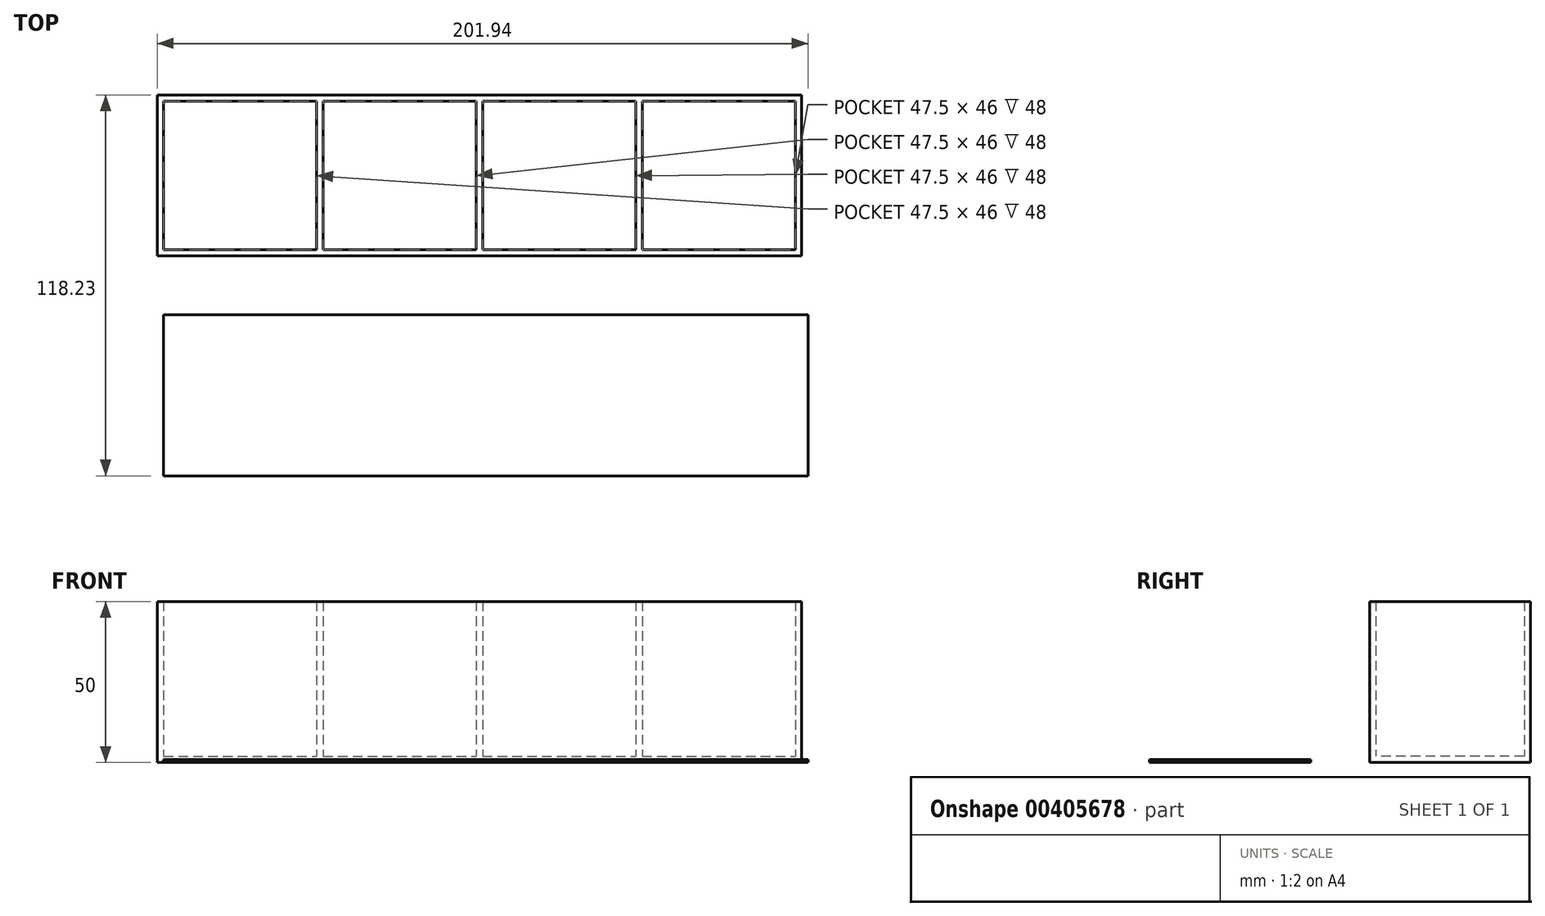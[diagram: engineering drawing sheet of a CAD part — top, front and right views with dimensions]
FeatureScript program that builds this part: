
annotation { "Feature Type Name" : "Feature", "Feature Type Description" : "" }
export const myFeature = defineFeature(function(context is Context, id is Id, definition is map)
    precondition{}
    {
        {
            var Q0;
            Q0=qCreatedBy(makeId("Top.planeOp"),FACE);
            var sketch = newSketch(context, id + "F0", { "sketchPlane" : qUnion([Q0])});
            skLineSegment(sketch, "E0.bottom", {"start": v(-100, 25) * mm, "end": v(100, 25) * mm});
            skLineSegment(sketch, "E0.top", {"start": v(-100, -25) * mm, "end": v(100, -25) * mm});
            skLineSegment(sketch, "E0.left", {"start": v(-100, 25) * mm, "end": v(-100, -25) * mm});
            skLineSegment(sketch, "E0.right", {"start": v(100, 25) * mm, "end": v(100, -25) * mm});
            skPoint(sketch, "E0.middle", {"position": v(0, 0) * mm});
            skLineSegment(sketch, "E1.bottom", {"start": v(-98, 23) * mm, "end": v(98, 23) * mm});
            skLineSegment(sketch, "E1.top", {"start": v(-98, -23) * mm, "end": v(98, -23) * mm});
            skLineSegment(sketch, "E1.left", {"start": v(-98, 23) * mm, "end": v(-98, -23) * mm});
            skLineSegment(sketch, "E1.right", {"start": v(98, 23) * mm, "end": v(98, -23) * mm});
            skLineSegment(sketch, "E2", {"start": v(50.5, 23) * mm, "end": v(50.5, -23) * mm});
            skLineSegment(sketch, "E3", {"start": v(48.5, -23) * mm, "end": v(48.5, 23) * mm});
            skLineSegment(sketch, "E4", {"start": v(1, 23) * mm, "end": v(1, -23) * mm});
            skLineSegment(sketch, "E5", {"start": v(-1, 23) * mm, "end": v(-1, -23) * mm});
            skLineSegment(sketch, "E6", {"start": v(-48.5, 23) * mm, "end": v(-48.5, -23) * mm});
            skLineSegment(sketch, "E7", {"start": v(-50.5, 23) * mm, "end": v(-50.5, -23) * mm});
            skSolve(sketch);
        }
        {
            var Q0;
            Q0 = qSketchRegion(id + "F0", true);
            var Q1;
            {var subQ0=sQuery(id+"F0.wireOp",EDGE,"E6");Q1=makeQuery(id+"F0.imprint","IMPRINT",FACE,{"disambiguationData":[TD([[makeQuery(id+"F0.imprint","IMPRINT",EDGE,{"derivedFrom":subQ0}),-1.0]])]});}
            var Q2;
            {var subQ0=sQuery(id+"F0.wireOp",EDGE,"E4");Q2=makeQuery(id+"F0.imprint","IMPRINT",FACE,{"disambiguationData":[TD([[makeQuery(id+"F0.imprint","IMPRINT",EDGE,{"derivedFrom":subQ0}),-1.0]])]});}
            var Q3;
            {var subQ0=sQuery(id+"F0.wireOp",EDGE,"E2");Q3=makeQuery(id+"F0.imprint","IMPRINT",FACE,{"disambiguationData":[TD([[makeQuery(id+"F0.imprint","IMPRINT",EDGE,{"derivedFrom":subQ0}),-1.0]])]});}
            extrude(context, id + "F1", {"entities" : qUnion([Q0, Q1, Q2, Q3]), "depth" : 50 * mm});
        }
        {
            var Q0;
            {var subQ0=sQuery(id+"F0.wireOp",EDGE,"E1.left");Q0=makeQuery(id+"F0.imprint","IMPRINT",FACE,{"disambiguationData":[TD([[makeQuery(id+"F0.imprint","IMPRINT",EDGE,{"derivedFrom":subQ0}),1.0]])]});}
            var Q1;
            {var subQ0=sQuery(id+"F0.wireOp",EDGE,"E5");Q1=makeQuery(id+"F0.imprint","IMPRINT",FACE,{"disambiguationData":[TD([[makeQuery(id+"F0.imprint","IMPRINT",EDGE,{"derivedFrom":subQ0}),-1.0]])]});}
            var Q2;
            {var subQ0=sQuery(id+"F0.wireOp",EDGE,"E3");Q2=makeQuery(id+"F0.imprint","IMPRINT",FACE,{"disambiguationData":[TD([[makeQuery(id+"F0.imprint","IMPRINT",EDGE,{"derivedFrom":subQ0}),1.0]])]});}
            var Q3;
            {var subQ0=sQuery(id+"F0.wireOp",EDGE,"E1.right");Q3=makeQuery(id+"F0.imprint","IMPRINT",FACE,{"disambiguationData":[TD([[makeQuery(id+"F0.imprint","IMPRINT",EDGE,{"derivedFrom":subQ0}),-1.0]])]});}
            extrude(context, id + "F2", {"entities" : qUnion([Q0, Q1, Q2, Q3]), "operationType" : NewBodyOperationType.ADD, "depth" : 2 * mm});
        }
        {
            var Q0;
            Q0=qCreatedBy(makeId("Top.planeOp"),FACE);
            var sketch = newSketch(context, id + "F3", { "sketchPlane" : qUnion([Q0])});
            skPoint(sketch, "E8", {"position": v(-98.06, -43.23) * mm});
            skLineSegment(sketch, "E9.bottom", {"start": v(-98.06, -43.23) * mm, "end": v(101.94, -43.23) * mm});
            skLineSegment(sketch, "E9.top", {"start": v(-98.06, -93.23) * mm, "end": v(101.94, -93.23) * mm});
            skLineSegment(sketch, "E9.left", {"start": v(-98.06, -43.23) * mm, "end": v(-98.06, -93.23) * mm});
            skLineSegment(sketch, "E9.right", {"start": v(101.94, -43.23) * mm, "end": v(101.94, -93.23) * mm});
            skSolve(sketch);
        }
        {
            var Q0;
            Q0=makeQuery(id+"F3.imprint","IMPRINT",FACE,{"disambiguationData":[TD([[makeQuery(id+"F3.imprint","IMPRINT",EDGE,{"derivedFrom":sQuery(id+"F3.wireOp",EDGE,"E9.bottom")}),-1.0]])]});
            extrude(context, id + "F4", {"entities" : qUnion([Q0]), "depth" : 1 * mm});
        }
    });
